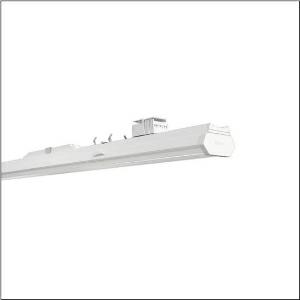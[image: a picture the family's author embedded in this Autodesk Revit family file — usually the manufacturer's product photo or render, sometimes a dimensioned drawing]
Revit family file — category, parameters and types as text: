
# Revit family: licross_r__11_protected_extreme_mo_51td1bdn49xge_f438
name_source: partatom
category: Lighting Fixtures
units: mm (PartAtom-declared; Revit-internal decimal feet)

## family parameters
Cut with Voids When Loaded = No
Host = Face
Light Source = No
Part Type = Normal
Room Calculation Point = No
Round Connector Dimension = Use Diameter
Shared = No

## types (1)
- --- (1 x LED, 9370 lm, 57.1 W, 4000K)
    Apparent Load = 57 VA
    CIE Flux Codes = 54 82 95 97 100
    Color Rendering = 80
    Color Temperature = 4000K
    Default Elevation = 1800 mm
    Description = Licross® 11 Protected extreme MO, luminaire insert, of sheet steel, galvanised, coil coated, white, length: 1.500mm, width: 90mm, height: 101mm, LED rated luminous flux: 9.370lm, light colour: 840, control gear: DALI 2, with plug, 5-pole, with phase selection, mains connection: 220..240V, AC, 50/60Hz, rated input power: 57W, halogen-free wiring, primary optical cover: cover, of PMMA, light emission: direct distribution, primary light characteristic: symmetric, protection rating (complete): IP54, insulation class (complete): insulation class I (protective earthing), certification: CE, ENEC, VDE, UKCA, protection symbol: D if used in an environment with non-conductive dust loads with corresponding accessories, impact resistance: IK06, permissible ambient temperature for indoor applications: -40..+45°C, corresponds to IFS (International Featured Standards) requirements for safety and quality in the food industry, reducing of maximum allowable ambient temperature of 5°C with ceiling mounting, LABS conformity tested according to VDMA 24364:2018-05, packaging unit: 1 piece
    Height = 92 mm
    Lamp = 1 x LED
    Lamp Light Flux = 9370 lm
    Lamp Power = 57.1 W
    Lamp count = 1
    Length = 1500 mm
    Luminous efficacy = 164 lm/W
    Manufacturer = Siteco
    ModVariant = No
    Model = 51TD1BDN49XGE
    Mounting Place = Ceiling
    Mounting Type = Pendant
    Number of Poles = 1
    OnlyDefault = Yes
    Power Factor = 1
    Product Name = Licross® 11 Protected extreme MO
    Product group = luminaire insert
    ProductGroupID = 902
    Protection Class = Protection class I
    Protection Degree = IP 54
    RLX_Detail_Level = 1
    RLX_Emergency_Light_Flux = 0 lm
    RLX_Emergency_Type = 0
    RLX_Emergency_Type_DB = No
    RlxData = <blob elided: 24265 chars, md5=5957fe07>
    Socket = socket
    Standby Power = 0 W
    System Light Flux = 9370 lm
    System Power = 57 W
    Type Comments = factory setting: luminous flux: 100 % | dim-lin: 254 | 378 mA
    Type Image = l_1256145.jpg
    URL = http://relux.com
    VarID = @adj_082742
    Voltage = 0 V
    Weight = 0.00 kg
    Width = 88 mm

## geometry (parser evidence)
native form markers: Blend x4, Sweep x11
no freeform markers — native parametric forms only
